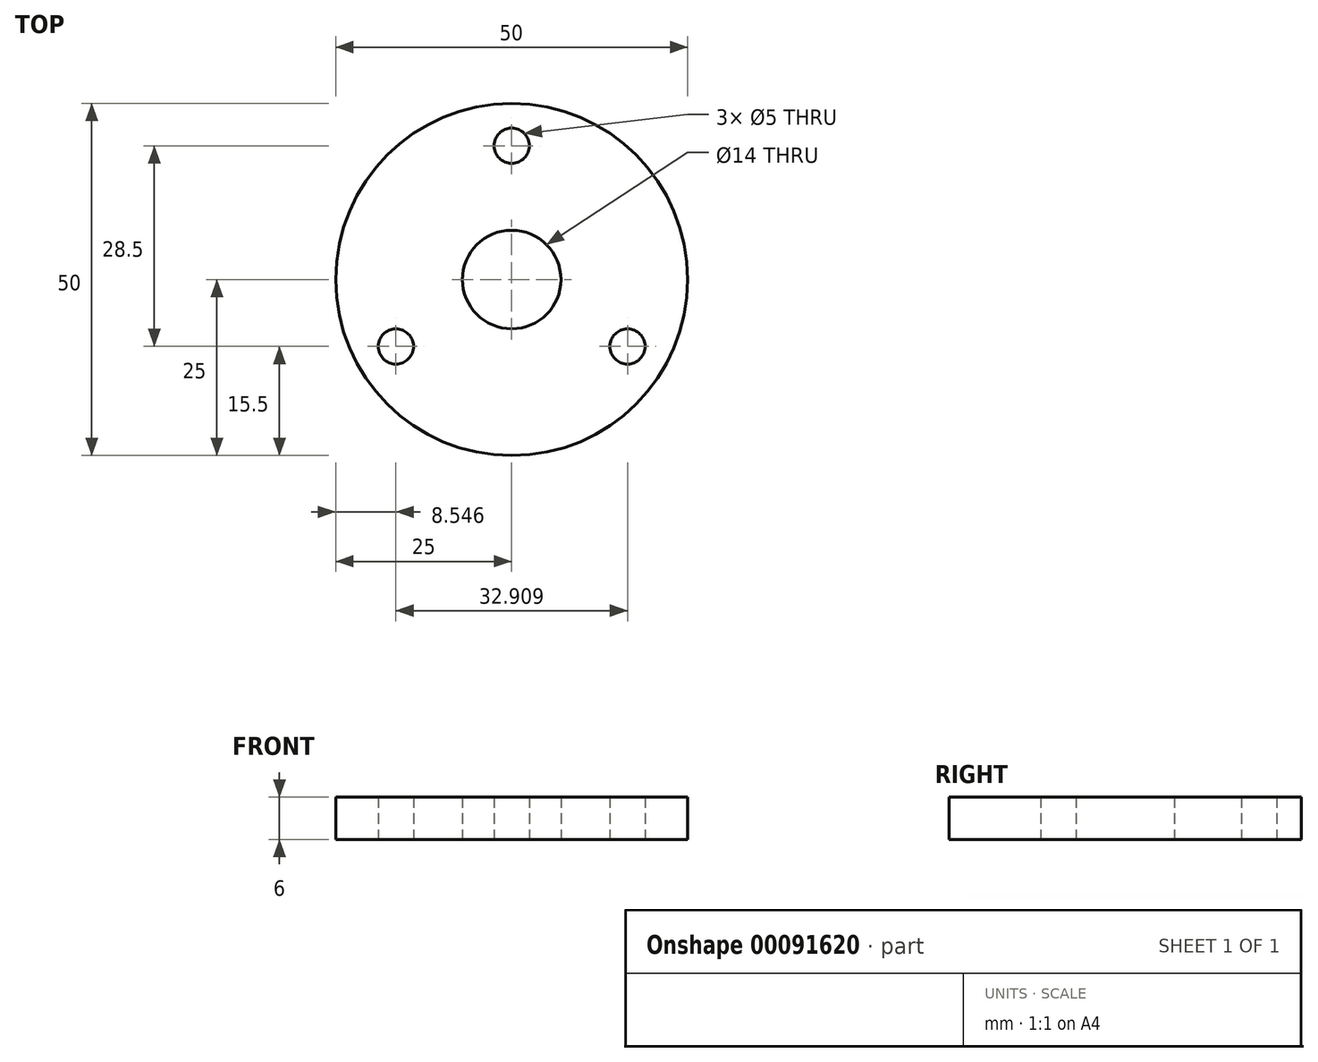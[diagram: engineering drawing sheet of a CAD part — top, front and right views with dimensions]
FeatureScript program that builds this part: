
annotation { "Feature Type Name" : "Feature", "Feature Type Description" : "" }
export const myFeature = defineFeature(function(context is Context, id is Id, definition is map)
    precondition{}
    {
        {
            var Q0;
            Q0=qCreatedBy(makeId("Top.planeOp"),FACE);
            var sketch = newSketch(context, id + "F0", { "sketchPlane" : qUnion([Q0])});
            skCircle(sketch, "E0", {"center": v(0, 0) * mm, "radius": 25 * mm});
            skCircle(sketch, "E1", {"center": v(0, 19) * mm, "radius": 2.5 * mm});
            skCircle(sketch, "E2.1.0", {"center": v(-16.45, -9.5) * mm, "radius": 2.5 * mm});
            skCircle(sketch, "E2.2.0", {"center": v(16.45, -9.5) * mm, "radius": 2.5 * mm});
            skCircle(sketch, "E3", {"center": v(0, 0) * mm, "radius": 7 * mm});
            skLineSegment(sketch, "E4", {"start": v(0, 0) * mm, "end": v(-16.45, -9.5) * mm, "construction": true});
            skLineSegment(sketch, "E5", {"start": v(0, 0) * mm, "end": v(16.45, -9.5) * mm, "construction": true});
            skSolve(sketch);
        }
        {
            var Q0;
            Q0=makeQuery(id+"F0.imprint","IMPRINT",FACE,{"disambiguationData":[TD([[makeQuery(id+"F0.imprint","IMPRINT",EDGE,{"derivedFrom":sQuery(id+"F0.wireOp",EDGE,"E0")}),1.0]])]});
            extrude(context, id + "F1", {"entities" : qUnion([Q0]), "depth" : 6 * mm});
        }
    });
